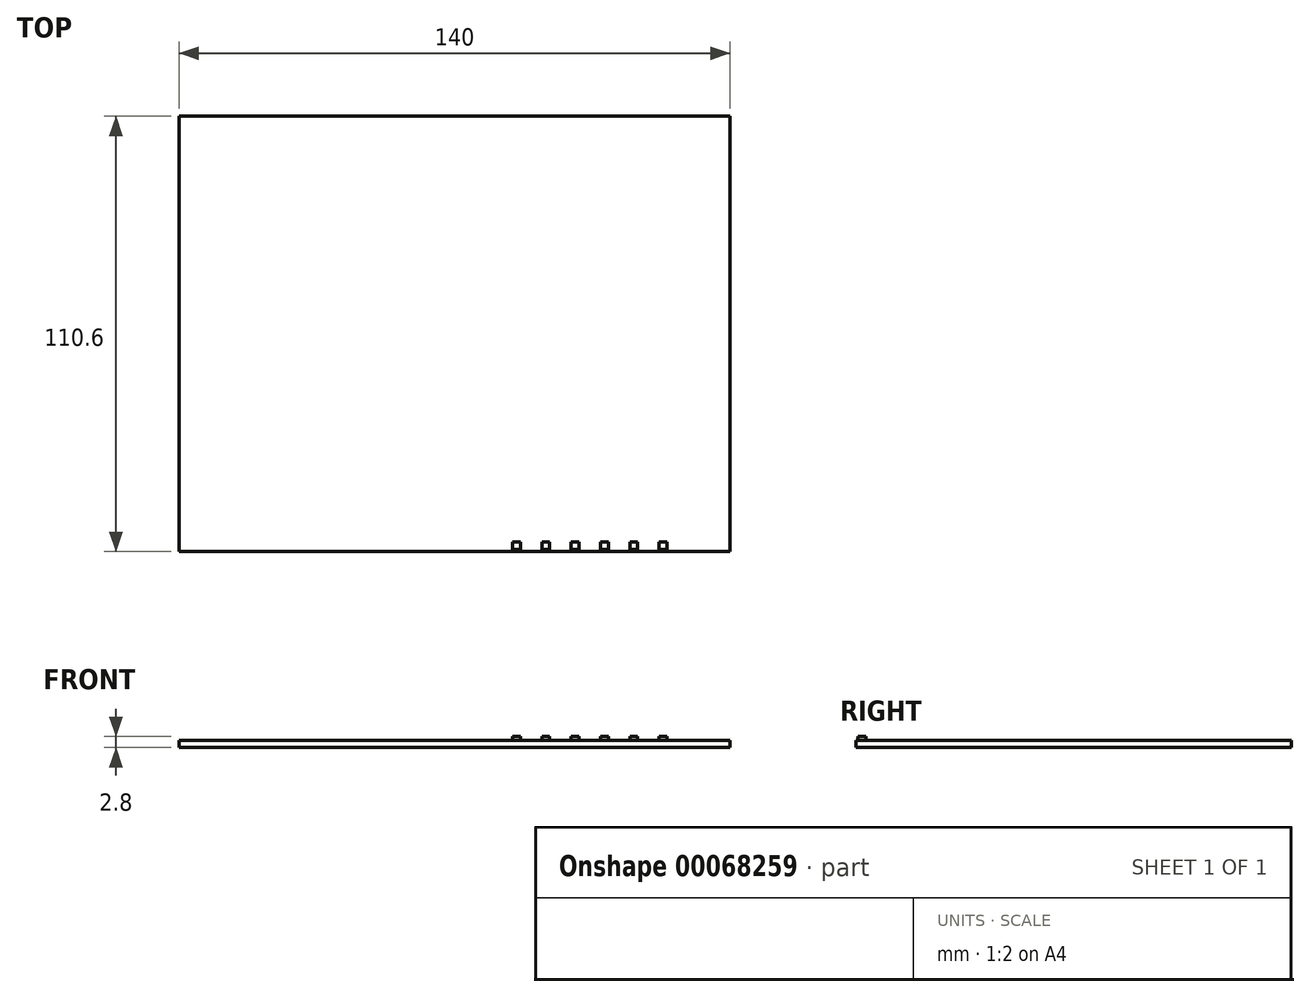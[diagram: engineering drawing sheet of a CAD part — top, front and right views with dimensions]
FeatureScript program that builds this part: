
annotation { "Feature Type Name" : "Feature", "Feature Type Description" : "" }
export const myFeature = defineFeature(function(context is Context, id is Id, definition is map)
    precondition{}
    {
        {
            var Q0;
            Q0=qCreatedBy(makeId("Top.planeOp"),FACE);
            var sketch = newSketch(context, id + "F0", { "sketchPlane" : qUnion([Q0])});
            skLineSegment(sketch, "E0.bottom", {"start": v(70, 55.3) * mm, "end": v(-70, 55.3) * mm});
            skLineSegment(sketch, "E0.top", {"start": v(70, -55.3) * mm, "end": v(-70, -55.3) * mm});
            skLineSegment(sketch, "E0.left", {"start": v(70, 55.3) * mm, "end": v(70, -55.3) * mm});
            skLineSegment(sketch, "E0.right", {"start": v(-70, 55.3) * mm, "end": v(-70, -55.3) * mm});
            skPoint(sketch, "E0.middle", {"position": v(0, 0) * mm});
            skSolve(sketch);
        }
        {
            var Q0;
            Q0 = qSketchRegion(id + "F0", true);
            extrude(context, id + "F1", {"entities" : qUnion([Q0]), "depth" : 1.8 * mm});
        }
        {
            var Q0;
            Q0=makeQuery(id+"F1.opExtrude","CAP_FACE",FACE,{"disambiguationData":[OSD([sQuery(id+"F0.wireOp",EDGE,"E0.bottom"),sQuery(id+"F0.wireOp",EDGE,"E0.top"),sQuery(id+"F0.wireOp",EDGE,"E0.left"),sQuery(id+"F0.wireOp",EDGE,"E0.right")])],"isStart":false});
            var sketch = newSketch(context, id + "F2", { "sketchPlane" : qUnion([Q0])});
            skLineSegment(sketch, "E1.bottom", {"start": v(52, -52.8) * mm, "end": v(54, -52.8) * mm});
            skLineSegment(sketch, "E1.top", {"start": v(52, -54.8) * mm, "end": v(54, -54.8) * mm});
            skLineSegment(sketch, "E1.left", {"start": v(52, -52.8) * mm, "end": v(52, -54.8) * mm});
            skLineSegment(sketch, "E1.right", {"start": v(54, -52.8) * mm, "end": v(54, -54.8) * mm});
            skLineSegment(sketch, "E2.1.0.0", {"start": v(46.55, -52.8) * mm, "end": v(46.55, -54.8) * mm});
            skLineSegment(sketch, "E2.1.0.1", {"start": v(44.55, -52.8) * mm, "end": v(44.55, -54.8) * mm});
            skLineSegment(sketch, "E2.1.0.2", {"start": v(44.55, -54.8) * mm, "end": v(46.55, -54.8) * mm});
            skLineSegment(sketch, "E2.1.0.3", {"start": v(44.55, -52.8) * mm, "end": v(46.55, -52.8) * mm});
            skLineSegment(sketch, "E2.2.0.0", {"start": v(39.1, -52.8) * mm, "end": v(39.1, -54.8) * mm});
            skLineSegment(sketch, "E2.2.0.1", {"start": v(37.1, -52.8) * mm, "end": v(37.1, -54.8) * mm});
            skLineSegment(sketch, "E2.2.0.2", {"start": v(37.1, -54.8) * mm, "end": v(39.1, -54.8) * mm});
            skLineSegment(sketch, "E2.2.0.3", {"start": v(37.1, -52.8) * mm, "end": v(39.1, -52.8) * mm});
            skLineSegment(sketch, "E2.3.0.0", {"start": v(31.65, -52.8) * mm, "end": v(31.65, -54.8) * mm});
            skLineSegment(sketch, "E2.3.0.1", {"start": v(29.65, -52.8) * mm, "end": v(29.65, -54.8) * mm});
            skLineSegment(sketch, "E2.3.0.2", {"start": v(29.65, -54.8) * mm, "end": v(31.65, -54.8) * mm});
            skLineSegment(sketch, "E2.3.0.3", {"start": v(29.65, -52.8) * mm, "end": v(31.65, -52.8) * mm});
            skLineSegment(sketch, "E2.4.0.0", {"start": v(24.2, -52.8) * mm, "end": v(24.2, -54.8) * mm});
            skLineSegment(sketch, "E2.4.0.1", {"start": v(22.2, -52.8) * mm, "end": v(22.2, -54.8) * mm});
            skLineSegment(sketch, "E2.4.0.2", {"start": v(22.2, -54.8) * mm, "end": v(24.2, -54.8) * mm});
            skLineSegment(sketch, "E2.4.0.3", {"start": v(22.2, -52.8) * mm, "end": v(24.2, -52.8) * mm});
            skLineSegment(sketch, "E2.5.0.0", {"start": v(16.75, -52.8) * mm, "end": v(16.75, -54.8) * mm});
            skLineSegment(sketch, "E2.5.0.1", {"start": v(14.75, -52.8) * mm, "end": v(14.75, -54.8) * mm});
            skLineSegment(sketch, "E2.5.0.2", {"start": v(14.75, -54.8) * mm, "end": v(16.75, -54.8) * mm});
            skLineSegment(sketch, "E2.5.0.3", {"start": v(14.75, -52.8) * mm, "end": v(16.75, -52.8) * mm});
            skLineSegment(sketch, "E2.direction1", {"start": v(54, -54.8) * mm, "end": v(46.55, -54.8) * mm, "construction": true});
            skSolve(sketch);
        }
        {
            var Q0;
            Q0 = qSketchRegion(id + "F2", true);
            extrude(context, id + "F3", {"entities" : qUnion([Q0]), "depth" : 1 * mm});
        }
    });
